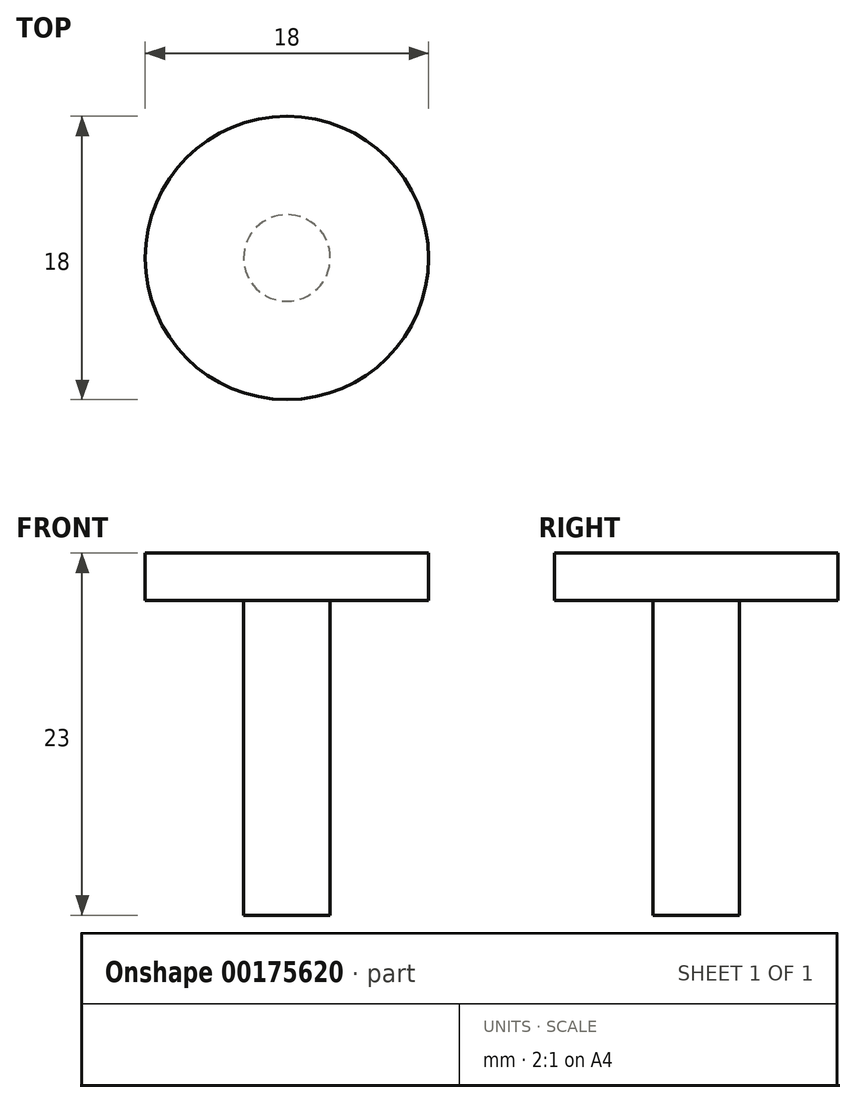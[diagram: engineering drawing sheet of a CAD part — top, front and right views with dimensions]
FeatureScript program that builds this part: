
annotation { "Feature Type Name" : "Feature", "Feature Type Description" : "" }
export const myFeature = defineFeature(function(context is Context, id is Id, definition is map)
    precondition{}
    {
        {
            var Q0;
            Q0=qCreatedBy(makeId("Front.planeOp"),FACE);
            var sketch = newSketch(context, id + "F0", { "sketchPlane" : qUnion([Q0])});
            skLineSegment(sketch, "E0", {"start": v(0, 9.05) * mm, "end": v(9, 9.05) * mm});
            skLineSegment(sketch, "E1", {"start": v(9, 9.05) * mm, "end": v(9, 6.05) * mm});
            skLineSegment(sketch, "E2", {"start": v(9, 6.05) * mm, "end": v(2.75, 6.05) * mm});
            skLineSegment(sketch, "E3", {"start": v(2.75, 6.05) * mm, "end": v(2.75, -13.95) * mm});
            skLineSegment(sketch, "E4", {"start": v(2.75, -13.95) * mm, "end": v(0, -13.95) * mm});
            skLineSegment(sketch, "E5", {"start": v(0, -13.95) * mm, "end": v(0, 9.05) * mm});
            skSolve(sketch);
        }
        {
            var Q0;
            Q0 = qSketchRegion(id + "F0", true);
            var Q1;
            Q1=sQuery(id+"F0.wireOp",EDGE,"E5");
            revolve(context, id + "F1", {"entities" : qUnion([Q0]), "axis" : qUnion([Q1]), "revolveType" : RevolveType.FULL});
        }
    });
